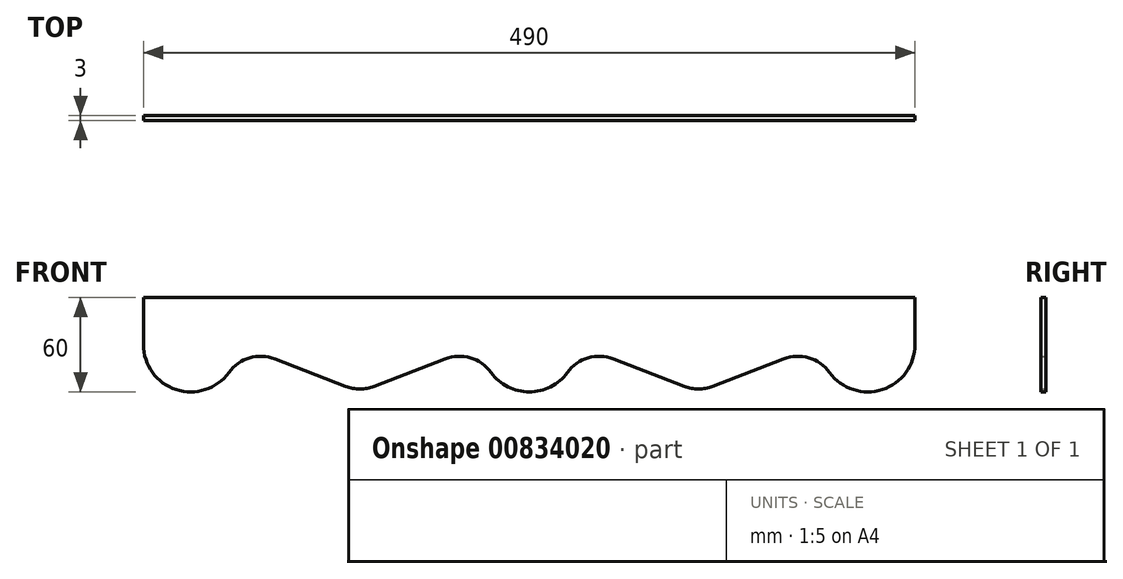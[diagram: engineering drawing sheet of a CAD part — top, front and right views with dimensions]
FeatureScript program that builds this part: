
annotation { "Feature Type Name" : "Feature", "Feature Type Description" : "" }
export const myFeature = defineFeature(function(context is Context, id is Id, definition is map)
    precondition{}
    {
        {
            var Q0;
            Q0=qCreatedBy(makeId("Front.planeOp"),FACE);
            var sketch = newSketch(context, id + "F0", { "sketchPlane" : qUnion([Q0])});
            skLineSegment(sketch, "E0.bottom", {"start": v(-245, 30) * mm, "end": v(245, 30) * mm});
            skLineSegment(sketch, "E0.left", {"start": v(-245, 30) * mm, "end": v(-245, 0) * mm});
            skLineSegment(sketch, "E0.right", {"start": v(245, 30) * mm, "end": v(245, 0) * mm});
            skPoint(sketch, "E0.middle", {"position": v(0, 0) * mm});
            skArc(sketch, "E1", {"start": v(-245, 0) * mm, "mid": v(-224.3, -28.52) * mm, "end": v(-190.76, -17.67) * mm});
            skArc(sketch, "E2", {"start": v(-24.24, -17.67) * mm, "mid": v(0, -30) * mm, "end": v(24.24, -17.67) * mm});
            skArc(sketch, "E3", {"start": v(190.76, -17.67) * mm, "mid": v(224.3, -28.52) * mm, "end": v(245, 0) * mm});
            skLineSegment(sketch, "E4", {"start": v(-161.53, -9.08) * mm, "end": v(-116.52, -26.5) * mm});
            skLineSegment(sketch, "E5", {"start": v(53.47, -9.08) * mm, "end": v(98.48, -26.5) * mm});
            skLineSegment(sketch, "E6", {"start": v(116.52, -26.5) * mm, "end": v(161.53, -9.08) * mm});
            skLineSegment(sketch, "E7", {"start": v(-98.48, -26.5) * mm, "end": v(-53.47, -9.08) * mm});
            skPoint(sketch, "E8.orphan", {"position": v(-245, -30) * mm});
            skPoint(sketch, "E9.orphan", {"position": v(245, -30) * mm});
            skPoint(sketch, "E10.visualSharp", {"position": v(-185, 0) * mm});
            skArc(sketch, "E10.filletArc", {"start": v(-161.53, -9.08) * mm, "mid": v(-177.6, -8.41) * mm, "end": v(-190.76, -17.67) * mm});
            skPoint(sketch, "E11.visualSharp", {"position": v(-107.5, -30) * mm});
            skArc(sketch, "E11.filletArc", {"start": v(-116.52, -26.5) * mm, "mid": v(-107.5, -28.2) * mm, "end": v(-98.48, -26.5) * mm});
            skPoint(sketch, "E12.visualSharp", {"position": v(-30, 0) * mm});
            skArc(sketch, "E12.filletArc", {"start": v(-24.24, -17.67) * mm, "mid": v(-37.4, -8.41) * mm, "end": v(-53.47, -9.08) * mm});
            skPoint(sketch, "E13.visualSharp", {"position": v(30, 0) * mm});
            skArc(sketch, "E13.filletArc", {"start": v(53.47, -9.08) * mm, "mid": v(37.4, -8.41) * mm, "end": v(24.24, -17.67) * mm});
            skPoint(sketch, "E14.visualSharp", {"position": v(107.5, -30) * mm});
            skArc(sketch, "E14.filletArc", {"start": v(98.48, -26.5) * mm, "mid": v(107.5, -28.2) * mm, "end": v(116.52, -26.5) * mm});
            skPoint(sketch, "E15.visualSharp", {"position": v(185, 0) * mm});
            skArc(sketch, "E15.filletArc", {"start": v(190.76, -17.67) * mm, "mid": v(177.6, -8.41) * mm, "end": v(161.53, -9.08) * mm});
            skSolve(sketch);
        }
        {
            var Q0;
            Q0=makeQuery(id+"F0.imprint","IMPRINT",FACE,{"disambiguationData":[TD([[makeQuery(id+"F0.imprint","IMPRINT",EDGE,{"derivedFrom":sQuery(id+"F0.wireOp",EDGE,"E0.bottom")}),-1.0]])]});
            extrude(context, id + "F1", {"entities" : qUnion([Q0]), "depth" : 3 * mm, "offsetDistance" : 25 * mm});
        }
    });
